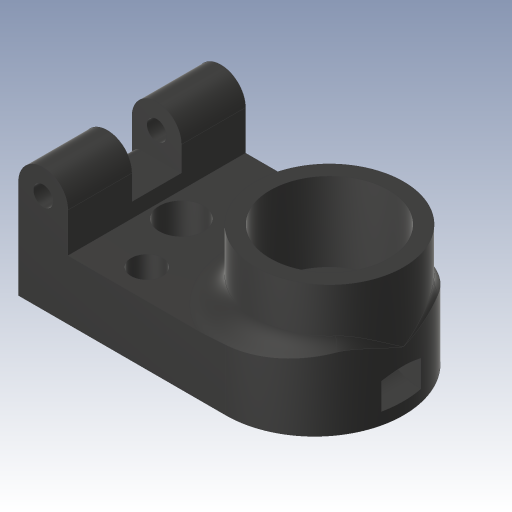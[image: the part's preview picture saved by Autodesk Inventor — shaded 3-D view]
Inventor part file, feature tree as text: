
AUTODESK INVENTOR PART (.ipt)
format: ipt  version: 2023.3 (Build 273359000, 359)  size: 298,496 bytes
history: native  units: in
note: dims shown in document units (in); Inventor stores cm internally (conversion verified against a paired STEP export)
features: sketch x7, extrude x4, hole x3, fillet x3, plane x2, sweep x1, projected_geometry x1
ambient origin geometry x8: Origin, YZ Plane, XZ Plane, XY Plane, X Axis, Y Axis, Z Axis, Center Point
bodies: Body1 (feature_tree)
feature tree (21):
  extrude  "Extrusion3"  Depth=0.1969in
  extrude  "Extrusion4"  Depth=0.7087in TaperAngle=0.0deg
  sketch  "Skizze6"  dims[d11=0.0984in d12=0.0787in]
  extrude  "Extrusion5"  Depth=0.0787in
  extrude  "Extrusion6"  Depth=0.1969in
  hole  "Bohrung1"  [1 undecoded]
  fillet  "Rundung2"  [1 undecoded]
  fillet  "Rundung3"  Radius=0.1969in
  fillet  "Rundung4"  Radius=0.5906in
  hole  "Bohrung2"  [1 undecoded]
  sketch  "Skizze8"  dims[d15=0.7087in d16=0.2559in d17=0.0in d18=0.0in d19=0.1969in d20=0.5906in]
  plane  "Arbeitsebene1"
  hole  "Bohrung3"  [1 undecoded]
  plane  "Arbeitsebene2"
  sweep  "Sweeping1"
  sketch  "Skizze3"  dims[d4=0.2362in d6=0.1969in]
  sketch  "Skizze5"  dims[d7=1.1811in d8=0.7087in d9=0.0in]
  sketch  "Skizze7"  dims[d13=0.1969in d14=0.1969in]
  projected_geometry  "Projizierte Kontur1"
  sketch  "Skizze10"  dims[d22=0.4724in d23=0.0591in]
  sketch  "Skizze11"  dims[d24=0.2756in d25=0.0in d26=0.0394in d27=0.0in d28=0.0984in d29=0.2362in d30=0.1772in d31=0.1575in d32=90.0deg d33=0.315in d34=0.0in d35=0.0984in d36=0.3543in d43=0.1575in d44=0.0394in d45=0.1969in d46=0.1181in d47=0.1181in d48=0.126in d49=0.2362in d50=0.1575in d51=0.0787in d52=90.0deg d53=0.315in d54=0.0in d55=0.1575in d57=0.0787in d58=0.1181in d66=0.1339in d67=0.2362in d68=0.2559in d69=0.1339in d70=90.0deg d71=0.2559in d72=0.0in d73=0.1378in d74=0.1575in d75=0.0in d76=0.0in d77=0.0394in]
note: 4 required parameter values undecoded (feature->parameter linkage not recoverable at this tier; creation-order binding heuristic only, values carry confidence <= 0.55)
